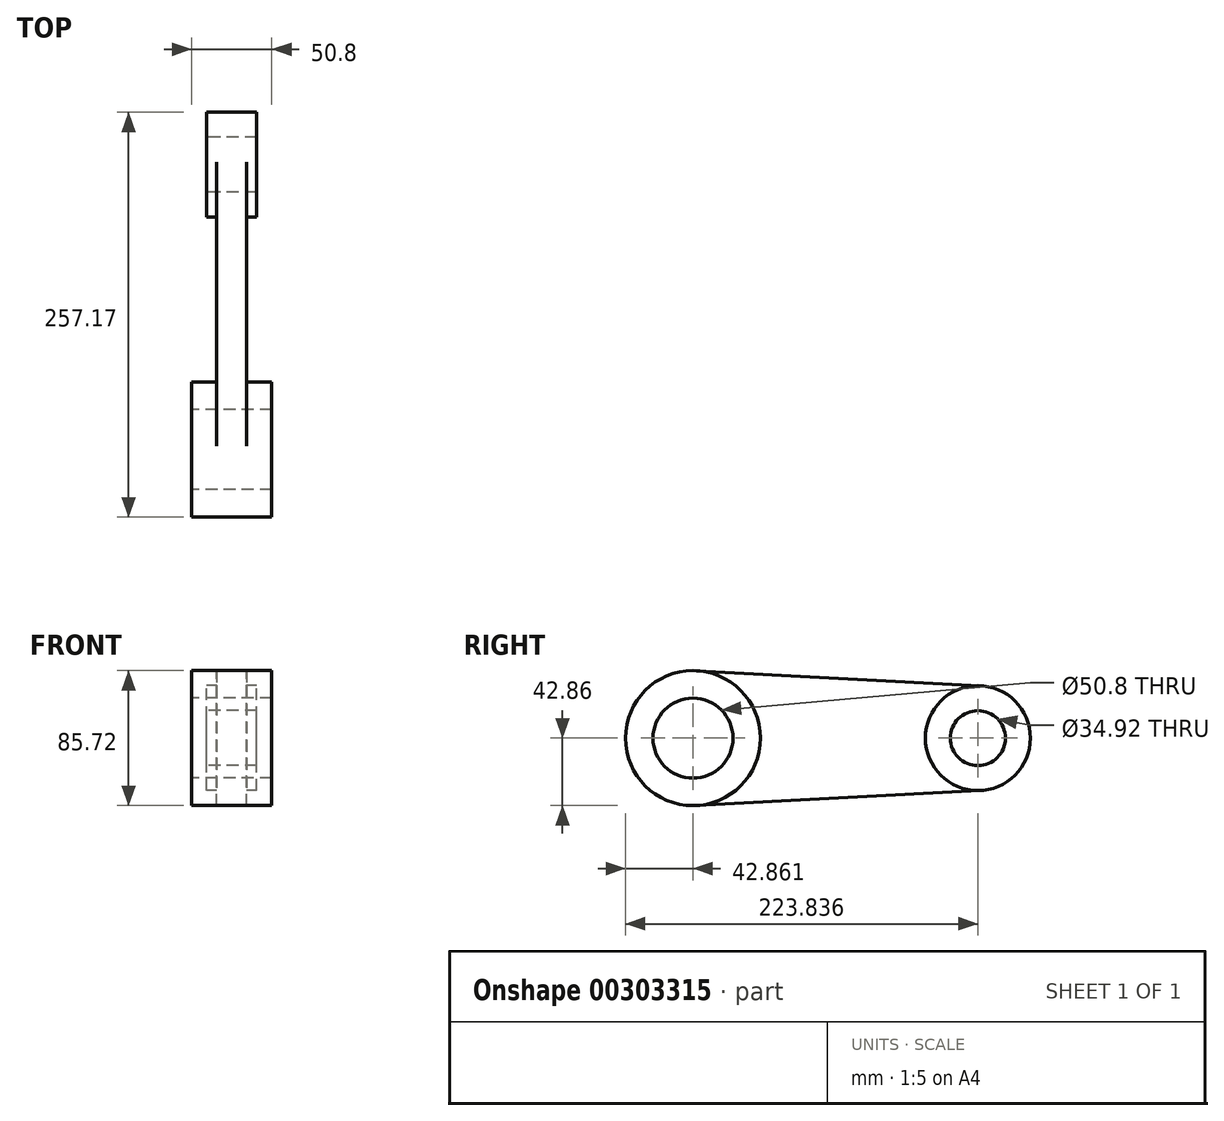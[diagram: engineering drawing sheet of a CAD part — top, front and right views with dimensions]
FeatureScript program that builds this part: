
annotation { "Feature Type Name" : "Feature", "Feature Type Description" : "" }
export const myFeature = defineFeature(function(context is Context, id is Id, definition is map)
    precondition{}
    {
        {
            var Q0;
            Q0=qCreatedBy(makeId("Right.planeOp"),FACE);
            var sketch = newSketch(context, id + "F0", { "sketchPlane" : qUnion([Q0])});
            skCircle(sketch, "E0", {"center": v(-38.18, 0) * mm, "radius": 25.4 * mm});
            skCircle(sketch, "E1", {"center": v(142.8, 0) * mm, "radius": 17.46 * mm});
            skCircle(sketch, "E2", {"center": v(-38.18, 0) * mm, "radius": 42.86 * mm});
            skCircle(sketch, "E3", {"center": v(142.8, 0) * mm, "radius": 33.34 * mm});
            skLineSegment(sketch, "E4", {"start": v(-35.92, -42.8) * mm, "end": v(144.55, -33.3) * mm});
            skLineSegment(sketch, "E5", {"start": v(-35.92, 42.8) * mm, "end": v(144.55, 33.3) * mm});
            skSolve(sketch);
        }
        {
            var Q0;
            {var subQ0=sQuery(id+"F0.wireOp",EDGE,"E4");Q0=makeQuery(id+"F0.imprint","IMPRINT",FACE,{"disambiguationData":[TD([[makeQuery(id+"F0.imprint","IMPRINT",EDGE,{"derivedFrom":subQ0}),1.0]])]});}
            extrude(context, id + "F1", {"entities" : qUnion([Q0]), "endBound" : BoundingType.SYMMETRIC, "depth" : 19.05 * mm});
        }
        {
            var Q0;
            Q0=makeQuery(id+"F0.imprint","IMPRINT",FACE,{"disambiguationData":[TD([[makeQuery(id+"F0.imprint","IMPRINT",EDGE,{"derivedFrom":sQuery(id+"F0.wireOp",EDGE,"E0")}),-1.0]])]});
            extrude(context, id + "F2", {"entities" : qUnion([Q0]), "operationType" : NewBodyOperationType.ADD, "endBound" : BoundingType.SYMMETRIC, "depth" : 50.8 * mm});
        }
        {
            var Q0;
            Q0=makeQuery(id+"F0.imprint","IMPRINT",FACE,{"disambiguationData":[TD([[makeQuery(id+"F0.imprint","IMPRINT",EDGE,{"derivedFrom":sQuery(id+"F0.wireOp",EDGE,"E1")}),-1.0]])]});
            extrude(context, id + "F3", {"entities" : qUnion([Q0]), "operationType" : NewBodyOperationType.ADD, "endBound" : BoundingType.SYMMETRIC, "depth" : 31.75 * mm});
        }
    });
